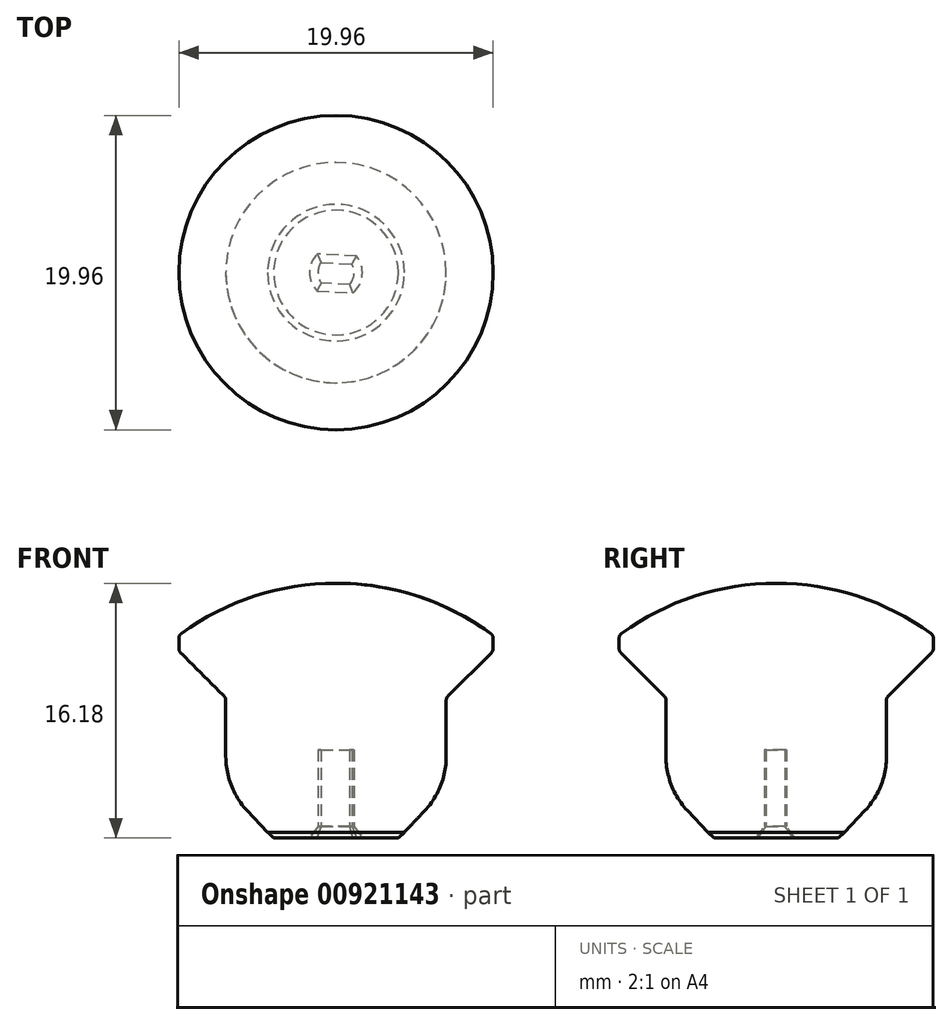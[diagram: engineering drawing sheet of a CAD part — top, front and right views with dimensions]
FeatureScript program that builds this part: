
annotation { "Feature Type Name" : "Feature", "Feature Type Description" : "" }
export const myFeature = defineFeature(function(context is Context, id is Id, definition is map)
    precondition{}
    {
        {
            var Q0;
            Q0=qCreatedBy(makeId("Front.planeOp"),FACE);
            var sketch = newSketch(context, id + "F0", { "sketchPlane" : qUnion([Q0])});
            skLineSegment(sketch, "E0", {"start": v(7, 3.18) * mm, "end": v(7, 8.9) * mm});
            skCircle(sketch, "E1", {"center": v(0, -0.56) * mm, "radius": 16.74 * mm});
            skPoint(sketch, "E1.second.point", {"position": v(0, 16.18) * mm});
            skPoint(sketch, "E1.third.point", {"position": v(-2.27, -17.14) * mm});
            skLineSegment(sketch, "E2", {"start": v(0, 16.18) * mm, "end": v(0, 0) * mm});
            skPoint(sketch, "E3.end.orphan", {"position": v(5.8, 0) * mm});
            skLineSegment(sketch, "E4", {"start": v(7, 3.18) * mm, "end": v(4, 0) * mm});
            skLineSegment(sketch, "E5", {"start": v(4, 0) * mm, "end": v(0, 0) * mm});
            skLineSegment(sketch, "E6", {"start": v(9.98, 12.88) * mm, "end": v(9.98, 11.88) * mm});
            skLineSegment(sketch, "E7", {"start": v(9.98, 11.88) * mm, "end": v(7, 8.9) * mm});
            skSolve(sketch);
        }
        {
            var Q0;
            Q0=makeQuery(id+"F0.imprint","IMPRINT",FACE,{"disambiguationData":[TD([[makeQuery(id+"F0.imprint","IMPRINT",EDGE,{"derivedFrom":sQuery(id+"F0.wireOp",EDGE,"E0")}),1.0]])]});
            var Q1;
            Q1=sQuery(id+"F0.wireOp",EDGE,"E2");
            revolve(context, id + "F1", {"surfaceOperationType" : NewSurfaceOperationType.NEW, "entities" : qUnion([Q0]), "axis" : qUnion([Q1]), "revolveType" : RevolveType.FULL});
        }
        {
            var Q0;
            Q0=makeQuery(id+"F1.opRevolve","SWEPT_FACE",FACE,{"disambiguationData":[OSD([sQuery(id+"F0.wireOp",EDGE,"E5")])]});
            var sketch = newSketch(context, id + "F2", { "sketchPlane" : qUnion([Q0])});
            skCircle(sketch, "E8", {"center": v(0, 0) * mm, "radius": 1.15 * mm});
            skLineSegment(sketch, "E9.top", {"start": v(-0.81, -0.86) * mm, "end": v(-0.77, -0.86) * mm});
            skLineSegment(sketch, "E9.left", {"start": v(-0.81, -0.82) * mm, "end": v(-0.81, -0.86) * mm});
            skLineSegment(sketch, "E10", {"start": v(-0.95, 0.66) * mm, "end": v(0.87, 0.75) * mm});
            skPoint(sketch, "E11.start.orphan", {"position": v(-0.87, 0.75) * mm});
            skLineSegment(sketch, "E12", {"start": v(-1.56, -0.68) * mm, "end": v(1.57, -0.51) * mm});
            skSolve(sketch);
        }
        {
            var Q0;
            {var subQ0=sQuery(id+"F2.wireOp",EDGE,"caEsol3X-vJNc-yw5V-LPCB-aK8iE5WneOSj");Q0=makeQuery(id+"F2.imprint","IMPRINT",FACE,{"disambiguationData":[TD([[makeQuery(id+"F2.imprint","IMPRINT",EDGE,{"derivedFrom":subQ0}),-1.0]])]});}
            var Q1;
            {var subQ0=sQuery(id+"F2.wireOp",EDGE,"E10");Q1=makeQuery(id+"F2.imprint","IMPRINT",FACE,{"disambiguationData":[TD([[makeQuery(id+"F2.imprint","IMPRINT",EDGE,{"derivedFrom":subQ0}),-1.0]])]});}
            extrude(context, id + "F3", {"entities" : qUnion([Q0, Q1]), "operationType" : NewBodyOperationType.REMOVE, "oppositeDirection" : true, "depth" : 5.6 * mm, "offsetDistance" : 25 * mm});
        }
        {
            var Q0;
            Q0=makeQuery(id+"F1.opRevolve","SWEPT_EDGE",EDGE,{"disambiguationData":[OSD([sQuery(id+"F0.wireOp",EDGE,"E0"),sQuery(id+"F0.wireOp",EDGE,"E7")])]});
            var Q1;
            Q1=makeQuery(id+"F1.opRevolve","SWEPT_EDGE",EDGE,{"disambiguationData":[OSD([sQuery(id+"F0.wireOp",EDGE,"E6"),sQuery(id+"F0.wireOp",EDGE,"E7")])]});
            var Q2;
            Q2=makeQuery(id+"F1.opRevolve","SWEPT_EDGE",EDGE,{"disambiguationData":[OSD([sQuery(id+"F0.wireOp",EDGE,"E1"),sQuery(id+"F0.wireOp",EDGE,"E6")])]});
            fillet(context, id + "F4", {"entities" : qUnion([Q0, Q1, Q2]), "radius" : 0.4 * mm, "tangentPropagation" : true, "allowEdgeOverflow" : false});
        }
        {
            var Q0;
            Q0=makeQuery(id+"F1.opRevolve","SWEPT_EDGE",EDGE,{"disambiguationData":[OSD([sQuery(id+"F0.wireOp",EDGE,"E0"),sQuery(id+"F0.wireOp",EDGE,"E4")])]});
            fillet(context, id + "F5", {"entities" : qUnion([Q0]), "radius" : 5 * mm, "tangentPropagation" : true, "allowEdgeOverflow" : false});
        }
        {
            var Q0;
            Q0=makeQuery(id+"F1.opRevolve","SWEPT_FACE",FACE,{"disambiguationData":[OSD([sQuery(id+"F0.wireOp",EDGE,"E5")])]});
            chamfer(context, id + "F6", {"entities" : qUnion([Q0]), "chamferType" : ChamferType.TWO_OFFSETS, "width1" : 0.5 * mm, "oppositeDirection" : false, "width2" : 0.04 * mm, "tangentPropagation" : true});
        }
    });
